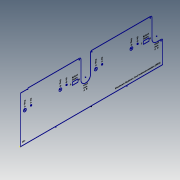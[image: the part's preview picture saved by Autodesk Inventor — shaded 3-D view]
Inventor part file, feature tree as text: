
AUTODESK INVENTOR PART (.ipt)
format: ipt  version: 2020.5 (Build 245400000, 400)  size: 202,240 bytes
history: native  units: mm
features: sketch x1
ambient origin geometry x8: Origin, YZ Plane, XZ Plane, XY Plane, X Axis, Y Axis, Z Axis, Center Point
feature tree (1):
  sketch  "Sketch34"  dims[d13=18.0mm d14=60.0mm d856=2.6mm d857=9.1mm d858=2.099988mm d859=6.7mm d860=45.55mm d861=45.050107mm d862=36.050101mm d863=46.020973mm d864=2.6mm d865=9.1mm d866=2.099988mm d867=6.7mm d868=45.55mm d869=4.949893mm d870=13.949899mm d871=46.020973mm d872=8.5mm d873=2.1mm d874=2.1mm d875=7.9mm d876=44.306mm d877=23.049893mm d878=22.749893mm d879=47.406mm d880=2.1mm d881=2.0mm d882=2.0mm d883=2.1mm d884=19.999893mm d885=40.256mm d886=40.256mm d887=31.999893mm d888=6.0mm d889=6.5mm d890=2.1mm d891=2.1mm d892=26.7mm d893=38.919893mm d894=38.669893mm d895=29.8mm d896=4.3mm d897=2.1mm d898=6.0mm d899=47.292893mm d900=2.7mm d901=63.873077mm d902=6.0mm d903=2.6mm d904=9.1mm d905=2.099988mm d906=6.7mm d907=45.55mm d908=45.050107mm d909=36.050101mm d910=46.020973mm d911=2.6mm d912=9.2mm d913=2.099988mm d914=6.7mm d915=45.55mm d916=4.949893mm d917=13.949899mm d918=46.020973mm d919=8.5mm d920=2.1mm d921=2.1mm d922=7.9mm d923=44.306mm d924=23.049893mm d925=22.749893mm d926=47.406mm d927=2.1mm d928=2.0mm d929=2.0mm d930=2.1mm d931=19.999893mm d932=40.256mm d933=40.256mm d934=31.999893mm d935=6.0mm d936=6.5mm d937=2.1mm d938=2.1mm d939=26.7mm d940=38.919893mm d941=38.669893mm d942=29.8mm d943=147.392893mm d944=2.1mm d945=5.4mm d946=39.219893mm d947=23.6mm d948=2.1mm d949=5.5mm d950=39.219893mm d951=23.6mm]
